# Revit family: ACCU 20 (22, 26, 28) mDCI
name_source: partatom
category: Оборудование
units: mm (PartAtom-declared; Revit-internal decimal feet)

## family parameters
Всегда вертикально = Да
На основе рабочей плоскости = Нет
Общий = Нет
При загрузке вырезать с полостями = Нет
Размер круглого соединителя = Использовать диаметр
Тип детали = Нормальный
Точка расчета площади = Нет

## types (4) — shared parameters
ADSK_Версия Revit = 2017
ADSK_Завод-изготовитель = Altair
ADSK_Количество фаз = 3
ADSK_Масса = 115
ADSK_Материал = Корпус белый
ADSK_Наименование = Компрессорно-конденсаторный блок
ADSK_Напряжение = 380 В
ADSK_Размер_Высота = 1327 мм
ADSK_Размер_Глубина = 320 мм
ADSK_Размер_Ширина = 902 мм
D_газ = 19.1 мм
D_жидкость = 9.52 мм
H_опор = 29 мм
ЗО сверху от объекта = 600 мм
ЗО сзади от объекта = 300 мм
ЗО слева от объекта = 300 мм
ЗО спереди от объекта = 3000 мм
ЗО справа от объекта = 600 мм
Расстояние до верха решетки = 71 мм
zero-valued in all types: ЗО снизу от объекта, Отметка по умолчанию

## per-type parameters (varying)
| type | ADSK_Номинальная мощность | ADSK_Ток | ADSK_Холодильная мощность |
| ACCU 20 mDCI | 5130 Вт | 21 А | 20000 Вт |
| ACCU 22 mDCI | 5930 Вт | 23 А | 22400 Вт |
| ACCU 26 mDCI | 7430 Вт | 25 А | 26000 Вт |
| ACCU 28 mDCI | 8240 Вт | 26 А | 28000 Вт |

note: column(s) folded — value = type name in every type: ADSK_Марка
